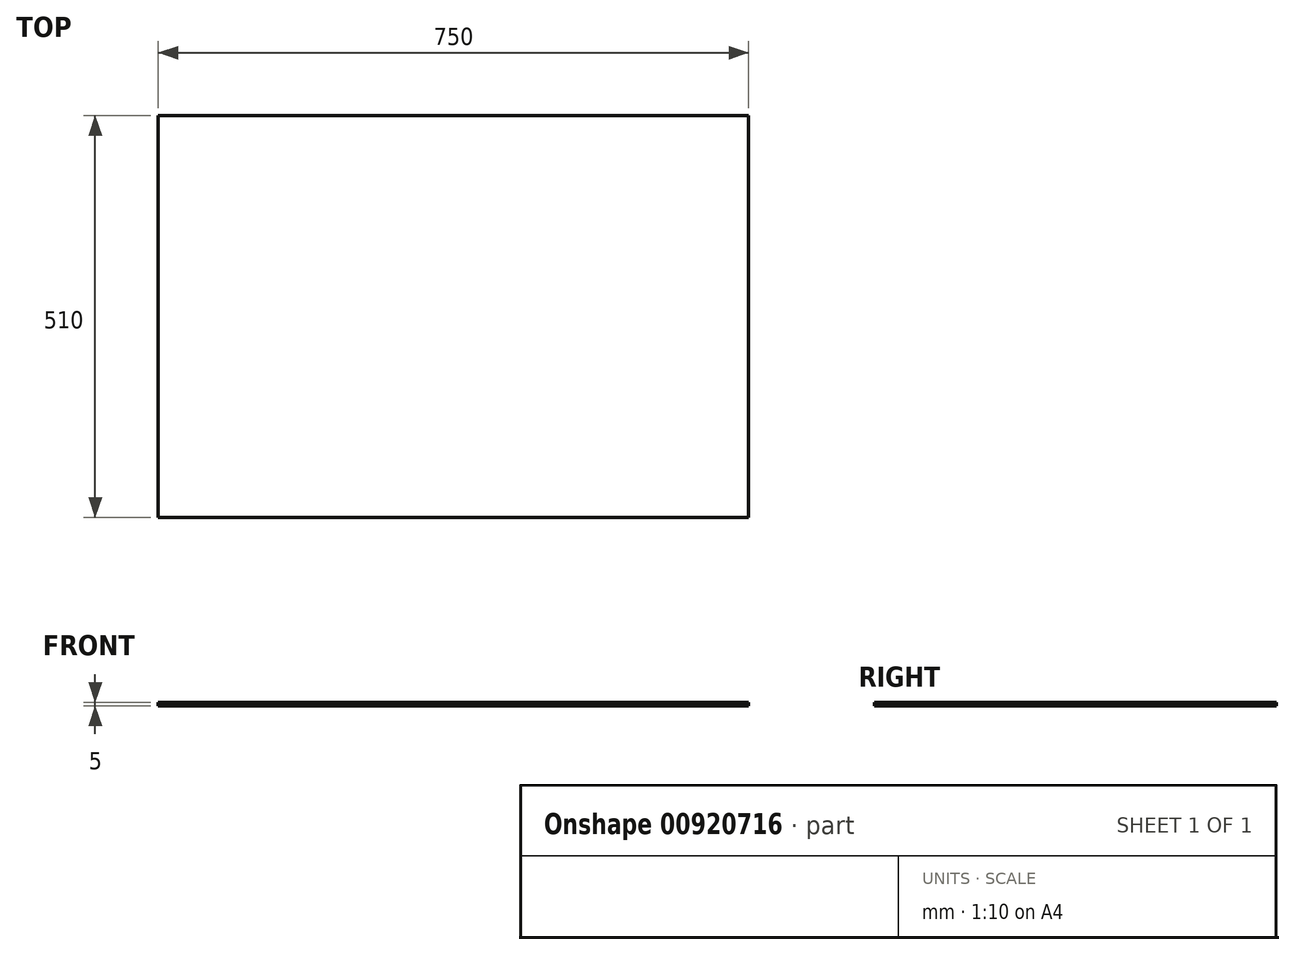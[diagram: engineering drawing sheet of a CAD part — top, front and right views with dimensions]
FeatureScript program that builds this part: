
annotation { "Feature Type Name" : "Feature", "Feature Type Description" : "" }
export const myFeature = defineFeature(function(context is Context, id is Id, definition is map)
    precondition{}
    {
        {
            var Q0;
            Q0=qCreatedBy(makeId("Top.planeOp"),FACE);
            var sketch = newSketch(context, id + "F0", { "sketchPlane" : qUnion([Q0])});
            skLineSegment(sketch, "E0.bottom", {"start": v(375, 255) * mm, "end": v(-375, 255) * mm});
            skLineSegment(sketch, "E0.top", {"start": v(375, -255) * mm, "end": v(-375, -255) * mm});
            skLineSegment(sketch, "E0.left", {"start": v(375, 255) * mm, "end": v(375, -255) * mm});
            skLineSegment(sketch, "E0.right", {"start": v(-375, 255) * mm, "end": v(-375, -255) * mm});
            skPoint(sketch, "E0.middle", {"position": v(0, 0) * mm});
            skSolve(sketch);
        }
        {
            var Q0;
            Q0=makeQuery(id+"F0.imprint","IMPRINT",FACE,{"disambiguationData":[TD([[makeQuery(id+"F0.imprint","IMPRINT",EDGE,{"derivedFrom":sQuery(id+"F0.wireOp",EDGE,"E0.bottom")}),1.0]])]});
            extrude(context, id + "F1", {"entities" : qUnion([Q0]), "depth" : 5 * mm, "offsetDistance" : 25 * mm});
        }
    });
